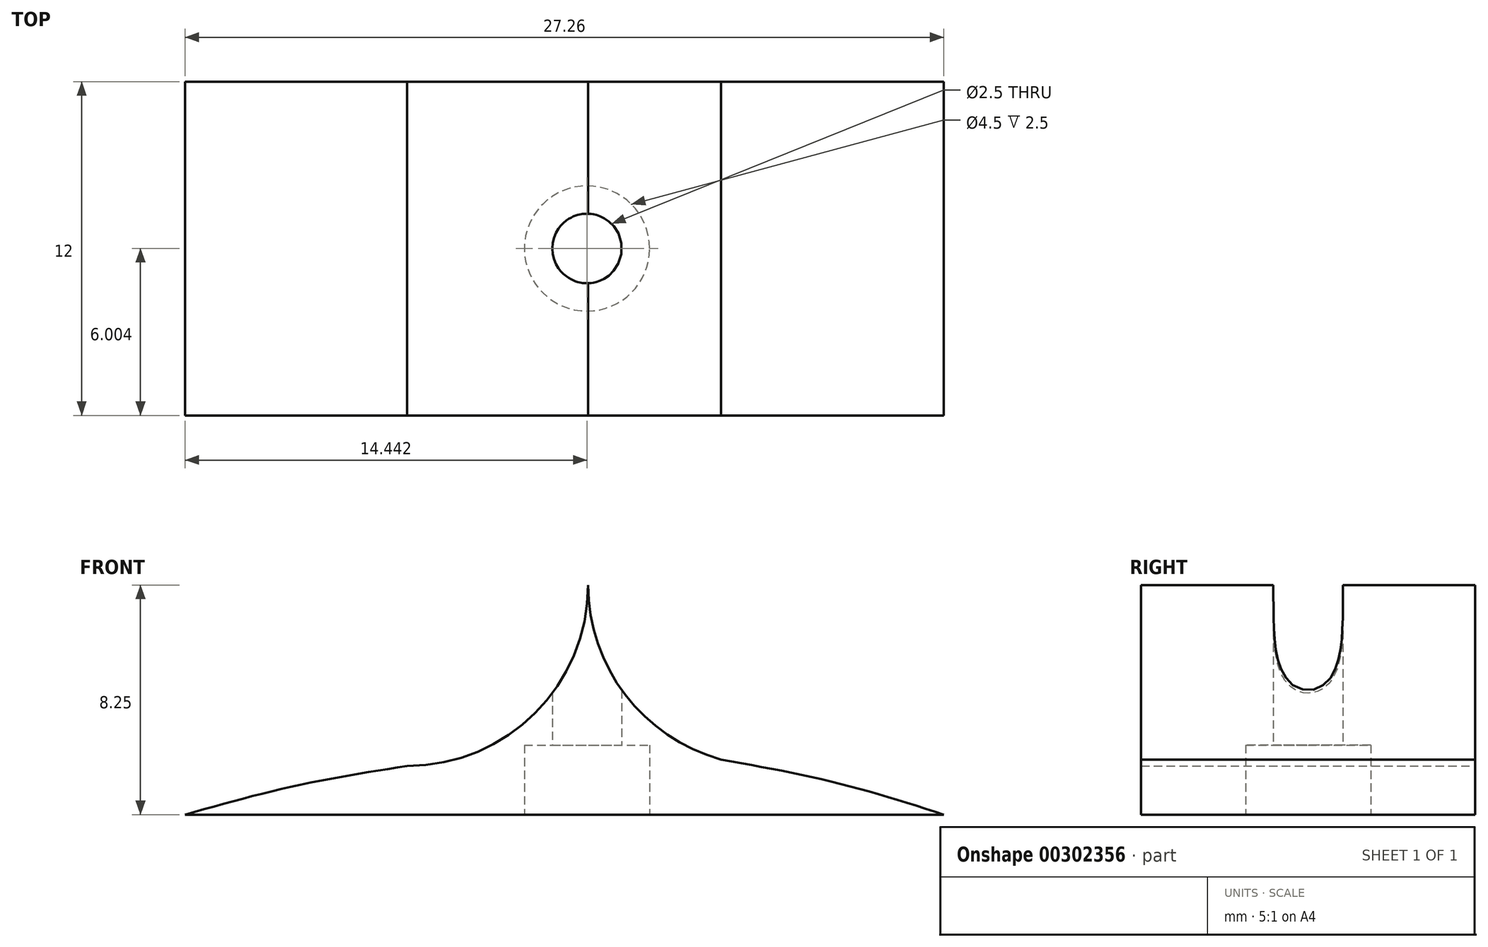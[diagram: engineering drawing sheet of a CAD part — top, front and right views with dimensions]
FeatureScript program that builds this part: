
annotation { "Feature Type Name" : "Feature", "Feature Type Description" : "" }
export const myFeature = defineFeature(function(context is Context, id is Id, definition is map)
    precondition{}
    {
        {
            var Q0;
            Q0=qCreatedBy(makeId("Front.planeOp"),FACE);
            var sketch = newSketch(context, id + "F0", { "sketchPlane" : qUnion([Q0])});
            skArc(sketch, "E0", {"start": v(-21.59, -6.5) * mm, "mid": v(-17, -4.6) * mm, "end": v(-15.09, 0) * mm});
            skArc(sketch, "E1", {"start": v(-15.09, 0) * mm, "mid": v(-13.76, -3.94) * mm, "end": v(-10.31, -6.27) * mm});
            skLineSegment(sketch, "E2", {"start": v(-21.59, -8.25) * mm, "end": v(-21.59, -6.5) * mm});
            skLineSegment(sketch, "E3", {"start": v(-10.31, -8.25) * mm, "end": v(-10.31, -6.27) * mm});
            skLineSegment(sketch, "E4", {"start": v(-21.59, -8.25) * mm, "end": v(-10.31, -8.25) * mm});
            skLineSegment(sketch, "E5", {"start": v(-21.59, -8.25) * mm, "end": v(-29.57, -8.25) * mm});
            skFitSpline(sketch, "E6", {"points": [v(-21.59, -6.5) * mm, v(-25.57, -7.2) * mm, v(-29.57, -8.25) * mm], "startDerivative": vector(-8.03, -1.26) * mm, "endDerivative": vector(-7.93, -2.24) * mm});
            skLineSegment(sketch, "E7", {"start": v(-10.31, -8.25) * mm, "end": v(-2.31, -8.25) * mm});
            skFitSpline(sketch, "E8", {"points": [v(-10.31, -6.27) * mm, v(-6.12, -7.12) * mm, v(-2.31, -8.25) * mm], "startDerivative": vector(8.34, -1.51) * mm, "endDerivative": vector(7.65, -2.46) * mm});
            skSolve(sketch);
        }
        {
            var Q0;
            Q0 = qSketchRegion(id + "F0", true);
            extrude(context, id + "F1", {"entities" : qUnion([Q0]), "depth" : 12 * mm});
        }
        {
            var Q0;
            Q0=makeQuery(id+"F1.opExtrude","SWEPT_FACE",FACE,{"disambiguationData":[OSD([sQuery(id+"F0.wireOp",EDGE,"E4"),sQuery(id+"F0.wireOp",EDGE,"E5"),sQuery(id+"F0.wireOp",EDGE,"E7")])]});
            var sketch = newSketch(context, id + "F2", { "sketchPlane" : qUnion([Q0])});
            skCircle(sketch, "E9", {"center": v(-15.13, 6) * mm, "radius": 1.25 * mm});
            skCircle(sketch, "E10", {"center": v(-15.13, 6) * mm, "radius": 2.25 * mm});
            skSolve(sketch);
        }
        {
            var Q0;
            Q0=makeQuery(id+"F2.imprint","IMPRINT",FACE,{"disambiguationData":[TD([[makeQuery(id+"F2.imprint","IMPRINT",EDGE,{"derivedFrom":sQuery(id+"F2.wireOp",EDGE,"E9")}),1.0]])]});
            extrude(context, id + "F3", {"entities" : qUnion([Q0]), "operationType" : NewBodyOperationType.REMOVE, "oppositeDirection" : true, "depth" : 25 * mm});
        }
        {
            var Q0;
            Q0=makeQuery(id+"F2.imprint","IMPRINT",FACE,{"disambiguationData":[TD([[makeQuery(id+"F2.imprint","IMPRINT",EDGE,{"derivedFrom":sQuery(id+"F2.wireOp",EDGE,"E9")}),-1.0]])]});
            extrude(context, id + "F4", {"entities" : qUnion([Q0]), "operationType" : NewBodyOperationType.REMOVE, "oppositeDirection" : true, "depth" : 2.5 * mm});
        }
    });
